# Revit family: Skylight-Wasco-Lean_To
name_source: partatom
category: Windows
revit_build: Autodesk Revit Architecture 2013 (Build: 20130531_2115(x64)
units: mm (PartAtom-declared; Revit-internal decimal feet)

## types (9) — shared parameters
Constraint = 1
Curb = Rubber, Black
Description = Skylight
Finish = Aluminum - Wasco - Aged Copper
Glazing 1 5_16 = No
Glazing Material = Glass - Wasco - Clear
Manufacturer = Wasco
Product Documentation Link = http://www.wascoskylights.com
Product Name = Lean-To
Product Page URL = http://www.wascoskylights.com
URL = http://www.wascoskylights.com

## per-type parameters (varying)
- Pinnacle 350 - 5/12: Angle=22.62°; Angle C=157.38°; C Lean To Width=12' - 2 7/32"; C Masking Region Depth=0' - 6 23/32"; Curb Height=0' - 4"; Curb Width=0' - 4"; Default Elevation=0' - 0"; Glazing Area=22.51 SF; Glazing Thickness=0' - 1 1/16"; Height=5' - 6 25/32"; Host Length=24' - 7"; Host Width=14' - 0"; Hypotenuse=7' - 11 1/4"; Lean To Height=5' - 0 29/32"; Lean To Height Offset=0' - 5 5/16"; Lean To Length=22' - 0"; Lean To Width=12' - 2 15/32"; Lean To Width Offset=0' - 2 7/32"; Length=22' - 7"; Masking Region Width=12' - 5 11/32"; Model=Pinnacle 350; Number of Purlins=2; Number of Rafters=4; Pinnacle=Base Plate - Sill : 350; Pinnacle 350=Yes; Pinnacle 600=No; Pinnacle 900=No; Pitch=5; Pitch 12 12=No; Pitch 5 12=Yes; Pitch 7 12=No; Pitch Actual=5; Purlin=Yes; Purlin Array Offset=1' - 8 27/32"; Rafter Array Offset=4' - 6 3/16"; Rafter Depth=0' - 5"; Rough Height=5' - 10 25/32"; Rough Width=12' - 2 15/32"; Side Height=5' - 1 11/32"; Side Height Offset=0' - 5 13/32"; Side Offset=0' - 5 13/16"; Sill Height Offset=0' - 0 17/32"; Sill Width Offset=0' - 3"; Width=12' - 0"; Width Actual=12' - 0"
- Pinnacle 600 - 5/12: Angle=22.62°; Angle C=157.38°; C Lean To Width=20' - 3 5/32"; C Masking Region Depth=0' - 7 21/32"; Curb Height=0' - 3 1/32"; Curb Width=0' - 4"; Default Elevation=20' - 6 11/32"; Glazing Area=64.06 SF; Glazing Thickness=0' - 1 3/16"; Height=9' - 1 15/32"; Host Length=42' - 0"; Host Width=22' - 0"; Hypotenuse=13' - 2 3/8"; Lean To Height=8' - 5 5/16"; Lean To Height Offset=0' - 7 5/8"; Lean To Length=39' - 5"; Lean To Width=20' - 3 13/32"; Lean To Width Offset=0' - 3 5/32"; Length=40' - 0"; Masking Region Width=20' - 7 1/4"; Model=Pinnacle 600; Number of Purlins=2; Number of Rafters=6; Pinnacle=Base Plate - Sill : 600; Pinnacle 350=No; Pinnacle 600=Yes; Pinnacle 900=No; Pitch=5; Pitch 12 12=No; Pitch 5 12=Yes; Pitch 7 12=No; Pitch Actual=5; Purlin=Yes; Purlin Array Offset=2' - 2 3/8"; Rafter Array Offset=5' - 8 9/16"; Rafter Depth=0' - 7 7/8"; Rough Height=9' - 4 1/2"; Rough Width=20' - 3 13/32"; Side Height=8' - 4 15/16"; Side Height Offset=0' - 8 17/32"; Side Offset=0' - 8 1/8"; Sill Height Offset=0' - 0 17/32"; Sill Width Offset=0' - 5 31/32"; Width=20' - 0"; Width Actual=20' - 0"
- Pinnacle 900 - 5/12: Angle=22.62°; Angle C=157.38°; C Lean To Width=28' - 4 3/16"; C Masking Region Depth=0' - 10 11/16"; Curb Height=0' - 3 1/32"; Curb Width=0' - 6"; Default Elevation=28' - 8 13/32"; Glazing Area=127.28 SF; Glazing Thickness=0' - 1 3/16"; Height=12' - 8 7/16"; Host Length=58' - 0"; Host Width=30' - 0"; Hypotenuse=18' - 5 3/4"; Lean To Height=11' - 9 3/4"; Lean To Height Offset=0' - 10 1/16"; Lean To Length=55' - 5"; Lean To Width=28' - 5 1/16"; Lean To Width Offset=0' - 4 3/16"; Length=56' - 0"; Masking Region Width=28' - 9 5/16"; Model=Pinnacle 900; Number of Purlins=4; Number of Rafters=6; Pinnacle=Base Plate - Sill : 900; Pinnacle 350=No; Pinnacle 600=No; Pinnacle 900=Yes; Pitch=5; Pitch 12 12=No; Pitch 5 12=Yes; Pitch 7 12=No; Pitch Actual=5; Purlin=Yes; Purlin Array Offset=3' - 0 15/16"; Rafter Array Offset=8' - 0"; Rafter Depth=0' - 10 3/4"; Rough Height=12' - 11 15/32"; Rough Width=28' - 5 1/16"; Side Height=11' - 8 25/32"; Side Height Offset=0' - 11 21/32"; Side Offset=0' - 10 21/32"; Sill Height Offset=0' - 0 5/8"; Sill Width Offset=0' - 6"; Width=28' - 0"; Width Actual=28' - 0"
- Pinnacle 350 - 7/12: Angle=30.26°; Angle C=149.74°; C Lean To Width=10' - 2 29/32"; C Masking Region Depth=0' - 7 13/32"; Curb Height=0' - 3 1/32"; Curb Width=0' - 4"; Default Elevation=10' - 5 13/16"; Glazing Area=18.61 SF; Glazing Thickness=0' - 1 1/16"; Height=6' - 5 7/32"; Host Length=22' - 0"; Host Width=12' - 0"; Hypotenuse=7' - 10 1/2"; Lean To Height=5' - 11 11/16"; Lean To Height Offset=0' - 4 31/32"; Lean To Length=19' - 5"; Lean To Width=10' - 3 5/32"; Lean To Width Offset=0' - 2 29/32"; Length=20' - 0"; Masking Region Width=10' - 6 21/32"; Model=Pinnacle 350; Number of Purlins=3; Number of Rafters=4; Pinnacle=Base Plate - Sill : 350; Pinnacle 350=Yes; Pinnacle 600=No; Pinnacle 900=No; Pitch=7; Pitch 12 12=No; Pitch 5 12=No; Pitch 7 12=Yes; Pitch Actual=7; Purlin=Yes; Purlin Array Offset=2' - 0 3/16"; Rafter Array Offset=4' - 0"; Rafter Depth=0' - 5"; Rough Height=6' - 8 1/4"; Rough Width=10' - 3 5/32"; Side Height=5' - 11 13/32"; Side Height Offset=0' - 5 25/32"; Side Offset=0' - 5 1/2"; Sill Height Offset=0' - 0 17/32"; Sill Width Offset=0' - 5 31/32"; Width=10' - 0"; Width Actual=10' - 0"
- Pinnacle 350 - 12/12: Angle=45.00°; Angle C=135.00°; C Lean To Width=9' - 4 1/8"; C Masking Region Depth=0' - 8 5/8"; Curb Height=0' - 3 1/32"; Curb Width=0' - 4"; Default Elevation=9' - 8 1/4"; Glazing Area=22.59 SF; Glazing Thickness=0' - 1 1/16"; Height=9' - 8 25/32"; Host Length=20' - 0"; Host Width=11' - 0"; Hypotenuse=10' - 5 13/32"; Lean To Height=9' - 4 1/8"; Lean To Height Offset=0' - 4 1/8"; Lean To Length=17' - 5"; Lean To Width=9' - 4 3/8"; Lean To Width Offset=0' - 4 1/8"; Length=18' - 0"; Masking Region Width=9' - 8 31/32"; Model=Pinnacle 350; Number of Purlins=2; Number of Rafters=4; Pinnacle=Base Plate - Sill : 350; Pinnacle 350=Yes; Pinnacle 600=No; Pinnacle 900=No; Pitch=12; Pitch 12 12=Yes; Pitch 5 12=No; Pitch 7 12=No; Pitch Actual=12; Purlin=Yes; Purlin Array Offset=2' - 6 9/16"; Rafter Array Offset=3' - 7 3/16"; Rafter Depth=0' - 5"; Rough Height=9' - 11 13/16"; Rough Width=9' - 4 3/8"; Side Height=9' - 1 23/32"; Side Height Offset=0' - 7 1/16"; Side Offset=0' - 4 5/8"; Sill Height Offset=0' - 0 17/32"; Sill Width Offset=0' - 5 31/32"; Width=9' - 0"; Width Actual=9' - 0"
- Pinnacle 600 - 7/12: Angle=30.26°; Angle C=149.74°; C Lean To Width=19' - 4 5/32"; C Masking Region Depth=0' - 8 21/32"; Curb Height=0' - 3 1/32"; Curb Width=0' - 4"; Default Elevation=19' - 8 5/16"; Glazing Area=68.97 SF; Glazing Thickness=0' - 1 3/16"; Height=11' - 11 3/32"; Host Length=40' - 0"; Host Width=21' - 0"; Hypotenuse=14' - 10 7/16"; Lean To Height=11' - 3 13/32"; Lean To Height Offset=0' - 7 1/8"; Lean To Length=37' - 5"; Lean To Width=19' - 4 13/32"; Lean To Width Offset=0' - 4 5/32"; Length=38' - 0"; Masking Region Width=19' - 9 5/32"; Model=Pinnacle 600; Number of Purlins=2; Number of Rafters=6; Pinnacle=Base Plate - Sill : 600; Pinnacle 350=No; Pinnacle 600=Yes; Pinnacle 900=No; Pitch=7; Pitch 12 12=No; Pitch 5 12=No; Pitch 7 12=Yes; Pitch Actual=7; Purlin=Yes; Purlin Array Offset=2' - 8 13/16"; Rafter Array Offset=5' - 5 5/32"; Rafter Depth=0' - 7 7/8"; Rough Height=12' - 2 1/8"; Rough Width=19' - 4 13/32"; Side Height=11' - 1 31/32"; Side Height Offset=0' - 9 1/8"; Side Offset=0' - 7 5/8"; Sill Height Offset=0' - 0 17/32"; Sill Width Offset=0' - 5 31/32"; Width=19' - 0"; Width Actual=19' - 0"
- Pinnacle 600 - 12/12: Angle=45.00°; Angle C=135.00°; C Lean To Width=15' - 5 29/32"; C Masking Region Depth=0' - 10 13/32"; Curb Height=0' - 3 1/32"; Curb Width=0' - 4"; Default Elevation=15' - 11 25/32"; Glazing Area=64.05 SF; Glazing Thickness=0' - 1 3/16"; Height=16' - 0 11/32"; Host Length=32' - 0"; Host Width=17' - 0"; Hypotenuse=17' - 3 29/32"; Lean To Height=15' - 5 29/32"; Lean To Height Offset=0' - 5 29/32"; Lean To Length=29' - 5"; Lean To Width=15' - 6 5/32"; Lean To Width Offset=0' - 5 29/32"; Length=30' - 0"; Masking Region Width=16' - 0 1/2"; Model=Pinnacle 600; Number of Purlins=2; Number of Rafters=6; Pinnacle=Base Plate - Sill : 600; Pinnacle 350=No; Pinnacle 600=Yes; Pinnacle 900=No; Pitch=12; Pitch 12 12=Yes; Pitch 5 12=No; Pitch 7 12=No; Pitch Actual=12; Purlin=No; Purlin Array Offset=3' - 0 3/8"; Rafter Array Offset=4' - 3 7/16"; Rafter Depth=0' - 7 7/8"; Rough Height=16' - 3 3/8"; Rough Width=15' - 6 5/32"; Side Height=15' - 1 3/16"; Side Height Offset=0' - 11 1/8"; Side Offset=0' - 6 13/32"; Sill Height Offset=0' - 0 17/32"; Sill Width Offset=0' - 5 31/32"; Width=15' - 0"; Width Actual=15' - 0"
- Pinnacle 900 - 7/12: Angle=30.26°; Angle C=149.74°; C Lean To Width=26' - 11 15/32"; C Masking Region Depth=0' - 11 31/32"; Curb Height=0' - 3 1/32"; Curb Width=0' - 6"; Default Elevation=27' - 4 29/32"; Glazing Area=135.85 SF; Glazing Thickness=0' - 1 3/16"; Height=16' - 6 21/32"; Host Length=55' - 0"; Host Width=28' - 6"; Hypotenuse=20' - 8 25/32"; Lean To Height=15' - 8 11/16"; Lean To Height Offset=0' - 9 11/32"; Lean To Length=52' - 5"; Lean To Width=27' - 0 11/32"; Lean To Width Offset=0' - 5 15/32"; Length=53' - 0"; Masking Region Width=27' - 5 25/32"; Model=Pinnacle 900; Number of Purlins=3; Number of Rafters=6; Pinnacle=Base Plate - Sill : 900; Pinnacle 350=No; Pinnacle 600=No; Pinnacle 900=Yes; Pitch=7; Pitch 12 12=No; Pitch 5 12=No; Pitch 7 12=Yes; Pitch Actual=7; Purlin=Yes; Purlin Array Offset=3' - 9 25/32"; Rafter Array Offset=7' - 6 27/32"; Rafter Depth=0' - 10 3/4"; Rough Height=16' - 9 11/16"; Rough Width=27' - 0 11/32"; Side Height=15' - 6 7/32"; Side Height Offset=1' - 0 7/16"; Side Offset=0' - 9 15/16"; Sill Height Offset=0' - 0 5/8"; Sill Width Offset=0' - 5 3/4"; Width=26' - 6"; Width Actual=26' - 6"
- Pinnacle 900 - 12/12: Angle=45.00°; Angle C=135.00°; C Lean To Width=22' - 7 17/32"; C Masking Region Depth=1' - 2 1/32"; Curb Height=0' - 3 1/32"; Curb Width=0' - 6"; Default Elevation=23' - 3 3/32"; Glazing Area=139.08 SF; Glazing Thickness=0' - 1 3/16"; Height=23' - 3 11/16"; Host Length=46' - 0"; Host Width=24' - 0"; Hypotenuse=25' - 3 25/32"; Lean To Height=22' - 7 17/32"; Lean To Height Offset=0' - 7 17/32"; Lean To Length=43' - 5"; Lean To Width=22' - 8 13/32"; Lean To Width Offset=0' - 7 17/32"; Length=44' - 0"; Masking Region Width=23' - 3 25/32"; Model=Pinnacle 900; Number of Purlins=2; Number of Rafters=6; Pinnacle=Base Plate - Sill : 900; Pinnacle 350=No; Pinnacle 600=No; Pinnacle 900=Yes; Pitch=14; Pitch 12 12=Yes; Pitch 5 12=No; Pitch 7 12=No; Pitch Actual=12; Purlin=Yes; Purlin Array Offset=4' - 5 11/32"; Rafter Array Offset=6' - 3 7/16"; Rafter Depth=0' - 10 3/4"; Rough Height=23' - 6 23/32"; Rough Width=22' - 8 13/32"; Side Height=22' - 0 1/2"; Side Height Offset=1' - 3 3/16"; Side Offset=0' - 8 1/8"; Sill Height Offset=0' - 0 5/8"; Sill Width Offset=0' - 5 31/32"; Width=22' - 0"; Width Actual=22' - 0"

## geometry (parser evidence)
native form markers: Blend x18, Sweep x46
no freeform markers — native parametric forms only
